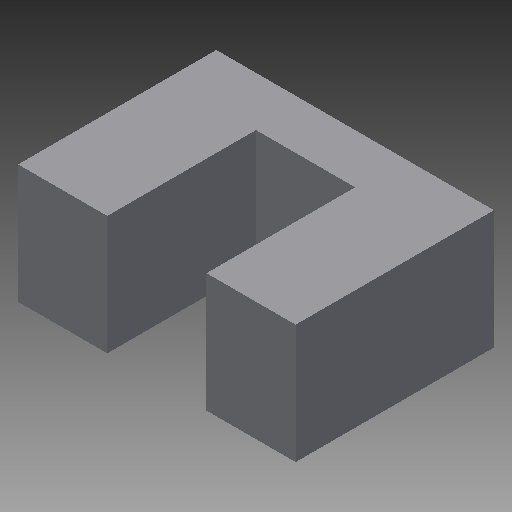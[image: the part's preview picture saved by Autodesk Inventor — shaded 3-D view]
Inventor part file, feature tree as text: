
AUTODESK INVENTOR PART (.ipt)
format: ipt  version: 2017 (Build 210142000, 142)  size: 90,112 bytes
history: native  units: mm
features: extrude x2, sketch x2
ambient origin geometry x8: Origin, YZ Plane, XZ Plane, XY Plane, X Axis, Y Axis, Z Axis, Center Point
bodies: Solid1 (feature_tree)
feature tree (4):
  extrude  "Extrusion1"  Depth=6.0mm
  extrude  "Extrusion2"  Depth=7.5mm TaperAngle=0.0deg
  sketch  "Sketch1"  dims[d0=14.0mm d1=6.0mm]
  sketch  "Sketch2"  dims[d2=10.0mm d3=0.0mm d6=7.5mm d7=0.0mm]
